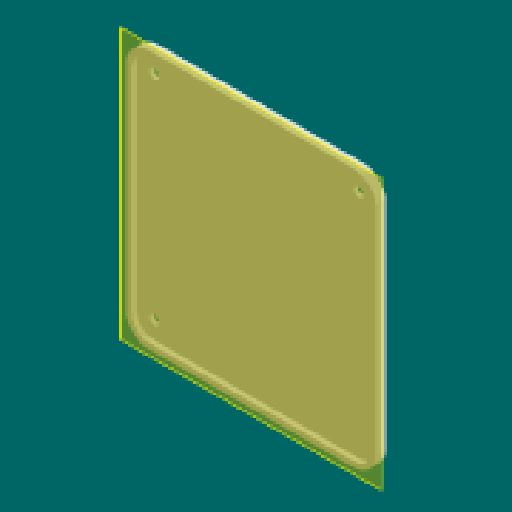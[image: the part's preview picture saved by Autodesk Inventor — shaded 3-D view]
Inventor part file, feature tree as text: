
AUTODESK INVENTOR PART (.ipt)
format: ipt  version: 2025.2 (Build 292293000, 293)  size: 147,968 bytes
history: native  units: mm
features: reference x12, sketch x4, extrude x4, plane x2, other x2
ambient origin geometry x8: Origin, YZ Plane, XZ Plane, XY Plane, X Axis, Y Axis, Z Axis, Center Point
bodies: Solid1 (feature_tree)
feature tree (24):
  plane  "Work Plane2"
  sketch  "Sketch2"  dims[d6=10.0mm d7=0.0mm d8=4.0mm]
  plane  "Work Plane3"
  extrude  "Extrusion3"  Depth=10.0mm
  extrude  "Extrusion4"  Depth=7.0mm TaperAngle=0.0deg
  extrude  "Extrusion5"  Depth=0.5mm
  extrude  "Extrusion6"  Depth=20.75mm
  reference  "Reference2"
  reference  "Reference3"
  reference  "Reference4"
  reference  "Reference5"
  reference  "Reference6"
  reference  "Reference7"
  reference  "Reference8"
  reference  "Reference9"
  reference  "Reference10"
  reference  "Reference11"
  reference  "Reference12"
  reference  "Reference13"
  sketch  "Sketch4"  dims[d10=3.2mm d11=7.0mm d12=0.0mm]
  sketch  "Sketch5"  dims[d15=0.5mm d16=0.5mm]
  sketch  "Sketch6"  dims[d17=0.5mm d18=0.5mm d19=7.0mm d20=0.0mm d21=20.75mm d22=0.0mm d23=0.0mm d24=0.0mm d25=0.0mm d26=0.0mm]
  other  "Assembly9"
  other  "BAS_Hardware:1"
